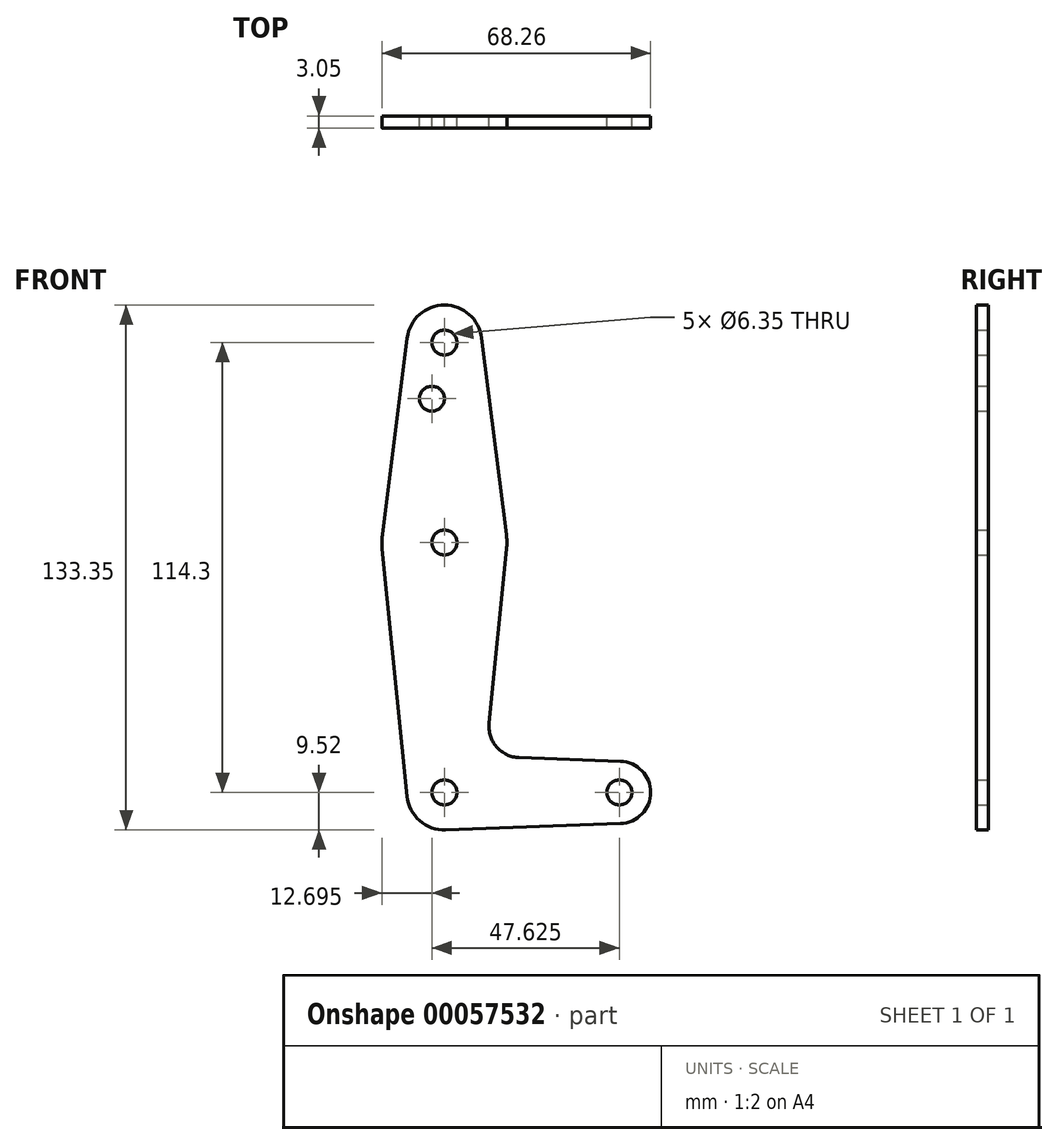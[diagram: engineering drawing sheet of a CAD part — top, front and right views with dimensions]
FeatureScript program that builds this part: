
annotation { "Feature Type Name" : "Feature", "Feature Type Description" : "" }
export const myFeature = defineFeature(function(context is Context, id is Id, definition is map)
    precondition{}
    {
        {
            var Q0;
            Q0=qCreatedBy(makeId("Front.planeOp"),FACE);
            var sketch = newSketch(context, id + "F0", { "sketchPlane" : qUnion([Q0])});
            skLineSegment(sketch, "E0", {"start": v(44.45, 0) * mm, "end": v(0, 0) * mm, "construction": true});
            skLineSegment(sketch, "E1", {"start": v(0, 0) * mm, "end": v(0, 114.3) * mm, "construction": true});
            skCircle(sketch, "E2", {"center": v(0, 114.3) * mm, "radius": 9.53 * mm});
            skCircle(sketch, "E3", {"center": v(0, 63.5) * mm, "radius": 15.88 * mm});
            skCircle(sketch, "E4", {"center": v(0, 0) * mm, "radius": 9.53 * mm});
            skCircle(sketch, "E5", {"center": v(44.45, 0) * mm, "radius": 7.94 * mm});
            skLineSegment(sketch, "E6", {"start": v(44.73, 7.93) * mm, "end": v(18.97, 8.85) * mm});
            skLineSegment(sketch, "E7", {"start": v(44.73, -7.93) * mm, "end": v(0.34, -9.52) * mm});
            skPoint(sketch, "E8.startSnap0", {"position": v(22.23, 0) * mm});
            skLineSegment(sketch, "E9", {"start": v(9.45, 115.5) * mm, "end": v(15.75, 65.48) * mm});
            skLineSegment(sketch, "E10", {"start": v(-9.45, 115.5) * mm, "end": v(-15.75, 65.48) * mm});
            skLineSegment(sketch, "E11", {"start": v(15.8, 61.91) * mm, "end": v(11.34, 17.6) * mm});
            skLineSegment(sketch, "E12", {"start": v(-15.8, 61.91) * mm, "end": v(-9.48, -0.95) * mm});
            skCircle(sketch, "E13", {"center": v(0, 114.3) * mm, "radius": 3.18 * mm});
            skCircle(sketch, "E14", {"center": v(0, 63.5) * mm, "radius": 3.18 * mm});
            skCircle(sketch, "E15", {"center": v(0, 0) * mm, "radius": 3.18 * mm});
            skCircle(sketch, "E16", {"center": v(44.45, 0) * mm, "radius": 3.18 * mm});
            skCircle(sketch, "E17", {"center": v(-3.18, 100.03) * mm, "radius": 3.18 * mm});
            skPoint(sketch, "E18.newPointB", {"position": v(0.34, 9.52) * mm});
            skArc(sketch, "E18.filletArc", {"start": v(11.34, 17.6) * mm, "mid": v(13.26, 11.57) * mm, "end": v(18.97, 8.85) * mm});
            skSolve(sketch);
        }
        {
            var Q0;
            Q0 = qSketchRegion(id + "F0", true);
            extrude(context, id + "F1", {"entities" : qUnion([Q0]), "depth" : 3.05 * mm});
        }
    });
